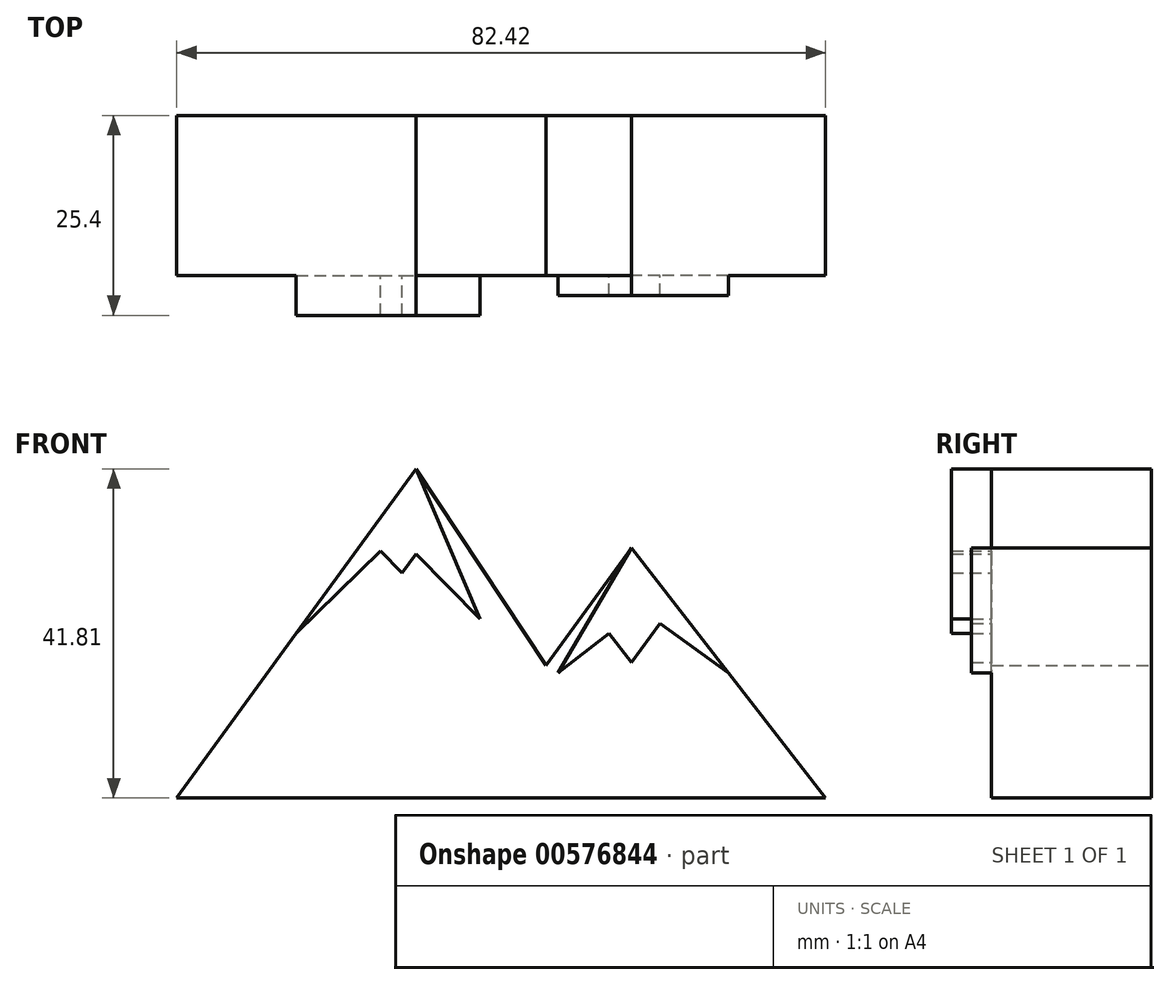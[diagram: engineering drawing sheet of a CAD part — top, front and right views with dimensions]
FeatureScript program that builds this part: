
annotation { "Feature Type Name" : "Feature", "Feature Type Description" : "" }
export const myFeature = defineFeature(function(context is Context, id is Id, definition is map)
    precondition{}
    {
        {
            var Q0;
            Q0=qCreatedBy(makeId("Front.planeOp"),FACE);
            var sketch = newSketch(context, id + "F0", { "sketchPlane" : qUnion([Q0])});
            skLineSegment(sketch, "E0", {"start": v(-8.12, 34.6) * mm, "end": v(-38.5, -7.22) * mm});
            skLineSegment(sketch, "E1", {"start": v(-8.12, 34.6) * mm, "end": v(8.42, 9.63) * mm});
            skLineSegment(sketch, "E2", {"start": v(8.42, 9.63) * mm, "end": v(19.25, 24.53) * mm});
            skLineSegment(sketch, "E3", {"start": v(19.25, 24.53) * mm, "end": v(43.92, -7.22) * mm});
            skLineSegment(sketch, "E4", {"start": v(43.92, -7.22) * mm, "end": v(-38.5, -7.22) * mm});
            skSolve(sketch);
        }
        {
            var Q0;
            Q0=makeQuery(id+"F0.imprint","IMPRINT",FACE,{"disambiguationData":[TD([[makeQuery(id+"F0.imprint","IMPRINT",EDGE,{"derivedFrom":sQuery(id+"F0.wireOp",EDGE,"E0")}),1.0]])]});
            extrude(context, id + "F1", {"entities" : qUnion([Q0]), "depth" : 25.4 * mm, "offsetDistance" : 25.4 * mm});
        }
        {
            var Q0;
            Q0=makeQuery(id+"F1.opExtrude","CAP_FACE",FACE,{"disambiguationData":[OSD([sQuery(id+"F0.wireOp",EDGE,"E0"),sQuery(id+"F0.wireOp",EDGE,"E1"),sQuery(id+"F0.wireOp",EDGE,"E2"),sQuery(id+"F0.wireOp",EDGE,"E3"),sQuery(id+"F0.wireOp",EDGE,"E4")])],"isStart":false});
            extrude(context, id + "F2", {"entities" : qUnion([Q0]), "operationType" : NewBodyOperationType.REMOVE, "oppositeDirection" : true, "depth" : 5.08 * mm, "offsetDistance" : 25.4 * mm});
        }
        {
            var Q0;
            Q0=makeQuery(id+"F2.boolean.opBoolean","COPY",FACE,{"derivedFrom":makeQuery(id+"F2.opExtrude","CAP_FACE",FACE,{"disambiguationData":[OSD([sQuery(id+"F0.wireOp",EDGE,"E0"),sQuery(id+"F0.wireOp",EDGE,"E1"),sQuery(id+"F0.wireOp",EDGE,"E2"),sQuery(id+"F0.wireOp",EDGE,"E3"),sQuery(id+"F0.wireOp",EDGE,"E4")])],"isStart":false})});
            var sketch = newSketch(context, id + "F3", { "sketchPlane" : qUnion([Q0])});
            skLineSegment(sketch, "E5", {"start": v(-8.12, 34.6) * mm, "end": v(-23.31, 13.69) * mm});
            skLineSegment(sketch, "E6", {"start": v(-23.31, 13.69) * mm, "end": v(-12.63, 24.14) * mm});
            skPoint(sketch, "E6.endSnap0", {"position": v(-15.72, 24.14) * mm});
            skLineSegment(sketch, "E7", {"start": v(-12.63, 24.14) * mm, "end": v(-9.9, 21.35) * mm});
            skLineSegment(sketch, "E8", {"start": v(-9.9, 21.35) * mm, "end": v(-8.12, 23.8) * mm});
            skLineSegment(sketch, "E9", {"start": v(-8.12, 23.8) * mm, "end": v(0, 15.5) * mm});
            skLineSegment(sketch, "E10", {"start": v(0, 15.5) * mm, "end": v(-8.12, 34.6) * mm});
            skLineSegment(sketch, "E11", {"start": v(-8.12, 34.6) * mm, "end": v(-8.12, 34.6) * mm});
            skLineSegment(sketch, "E12", {"start": v(-23.31, 13.69) * mm, "end": v(-15.72, 24.14) * mm});
            skSolve(sketch);
        }
        {
            var Q0;
            Q0=makeQuery(id+"F3.imprint","IMPRINT",FACE,{"disambiguationData":[TD([[makeQuery(id+"F3.imprint","IMPRINT",EDGE,{"derivedFrom":sQuery(id+"F3.wireOp",EDGE,"E5")}),1.0]])]});
            extrude(context, id + "F4", {"entities" : qUnion([Q0]), "operationType" : NewBodyOperationType.ADD, "depth" : 5.08 * mm, "offsetDistance" : 25.4 * mm});
        }
        {
            var Q0;
            Q0=makeQuery(id+"F2.boolean.opBoolean","COPY",FACE,{"derivedFrom":makeQuery(id+"F2.opExtrude","CAP_FACE",FACE,{"disambiguationData":[OSD([sQuery(id+"F0.wireOp",EDGE,"E0"),sQuery(id+"F0.wireOp",EDGE,"E1"),sQuery(id+"F0.wireOp",EDGE,"E2"),sQuery(id+"F0.wireOp",EDGE,"E3"),sQuery(id+"F0.wireOp",EDGE,"E4")])],"isStart":false})});
            var sketch = newSketch(context, id + "F5", { "sketchPlane" : qUnion([Q0])});
            skLineSegment(sketch, "E13", {"start": v(19.25, 24.53) * mm, "end": v(31.58, 8.65) * mm});
            skLineSegment(sketch, "E14", {"start": v(31.58, 8.65) * mm, "end": v(22.87, 14.98) * mm});
            skLineSegment(sketch, "E15", {"start": v(22.87, 14.98) * mm, "end": v(19.25, 10) * mm});
            skLineSegment(sketch, "E16", {"start": v(19.25, 10) * mm, "end": v(16.39, 13.69) * mm});
            skLineSegment(sketch, "E17", {"start": v(16.39, 13.69) * mm, "end": v(9.9, 8.65) * mm});
            skLineSegment(sketch, "E18", {"start": v(9.9, 8.65) * mm, "end": v(19.25, 24.53) * mm});
            skSolve(sketch);
        }
        {
            var Q0;
            Q0=makeQuery(id+"F5.imprint","IMPRINT",FACE,{"disambiguationData":[TD([[makeQuery(id+"F5.imprint","IMPRINT",EDGE,{"derivedFrom":sQuery(id+"F5.wireOp",EDGE,"E13")}),-1.0]])]});
            extrude(context, id + "F6", {"entities" : qUnion([Q0]), "operationType" : NewBodyOperationType.ADD, "depth" : 5.08 * mm, "offsetDistance" : 25.4 * mm});
        }
        {
            var Q0;
            Q0=makeQuery(id+"F6.opExtrude","CAP_FACE",FACE,{"disambiguationData":[OSD([sQuery(id+"F5.wireOp",EDGE,"E13"),sQuery(id+"F5.wireOp",EDGE,"E14"),sQuery(id+"F5.wireOp",EDGE,"E15"),sQuery(id+"F5.wireOp",EDGE,"E16"),sQuery(id+"F5.wireOp",EDGE,"E17"),sQuery(id+"F5.wireOp",EDGE,"E18")])],"isStart":false});
            extrude(context, id + "F7", {"entities" : qUnion([Q0]), "operationType" : NewBodyOperationType.REMOVE, "oppositeDirection" : true, "depth" : 2.54 * mm, "offsetDistance" : 25.4 * mm});
        }
    });
